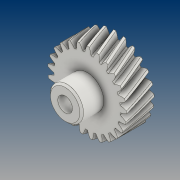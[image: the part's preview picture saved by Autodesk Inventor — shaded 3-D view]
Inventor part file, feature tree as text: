
AUTODESK INVENTOR PART (.ipt)
format: ipt  version: 2021 (Build 250183000, 183)  size: 522,752 bytes
history: native  units: mm (DEFAULTED — no unit token found)
features: extrude x3, plane x3, other x3, sketch x3, chamfer x1
ambient origin geometry x8: Origin, YZ Plane, XZ Plane, XY Plane, X Axis, Y Axis, Z Axis, Center Point
bodies: Solid1 (feature_tree)
feature tree (13):
  extrude  "Extrusion1"  Depth=15.0mm TaperAngle=0.0deg
  plane  "Work Plane2"
  plane  "Work Plane8"
  plane  "Work Plane9"
  other  "Spur Gear"
  sketch  "Sketch3"  dims[d16=60.0mm d17=0.0mm d34=1.256637mm d39=0.0mm d41=0.0mm d43=60.0mm d46=60.0mm d47=0.0mm d48=0.0mm d49=5.0mm d50=8.0mm d51=0.0mm d52=0.0mm d53=12.0mm d54=0.0mm d55=1.0mm d56=2.0mm d57=45.0deg]
  extrude  "Extrusion2"  Depth=10.0mm TaperAngle=0.0deg
  extrude  "Extrusion3"  Depth=1.256637mm TaperAngle=0.0deg
  chamfer  "Chamfer1"  [1 undecoded]
  sketch  "Sketch1"  dims[d0=42.9045mm d1=15.0mm d2=0.0mm]
  sketch  "Sketch2"  dims[d3=39.906666mm d4=10.0mm d5=0.0mm]
  other  "Srf1"
  other  "Pitch Diameter"
note: 1 required parameter value undecoded (feature->parameter linkage not recoverable at this tier; creation-order binding heuristic only, values carry confidence <= 0.55)
